# Revit family: RRHDWSSERFLN
name_source: partatom
category: Generic Models
revit_build: Autodesk Revit 2018 (Build: 20190510_1515(x64)
units: mm (PartAtom-declared; Revit-internal decimal feet)

## family parameters
Always vertical = No
Can host rebar = No
Cut with Voids When Loaded = No
Part Type = Normal
Room Calculation Point = No
Round Connector Dimension = Use Diameter
Shared = Yes
Work Plane-Based = Yes

## types (2) — shared parameters
Default Elevation = 48 "
Hardware Material = <By Category>
Inside Diameter = 0.313 "
Rod Radius = 0.1565 "

## per-type parameters (varying)
| type | Description | Height | Hex Width | Outside Diameter | Outside Radius | Top Diameter | Washer Height | Washer Lip Height |
| RRHDWSSERFLN1/2 | Serrated Flange Nut 304 1/2-13 | 0.45 " | 0.75 " | 1 " | 0.5 " | 0.8 " | 0.14 " | 0.05 " |
| RRHDWSSERFLN3/8 | Serrated Flange Nut 304 3/8-16 | 0.34 " | 0.56 " | 0.75 " | 0.375 " | 0.56 " | 0.11 " | 0.04 " |

note: column(s) folded — value = type name in every type: Catalog Number

## geometry (parser evidence)
native form markers: Sweep x3
no freeform markers — native parametric forms only
